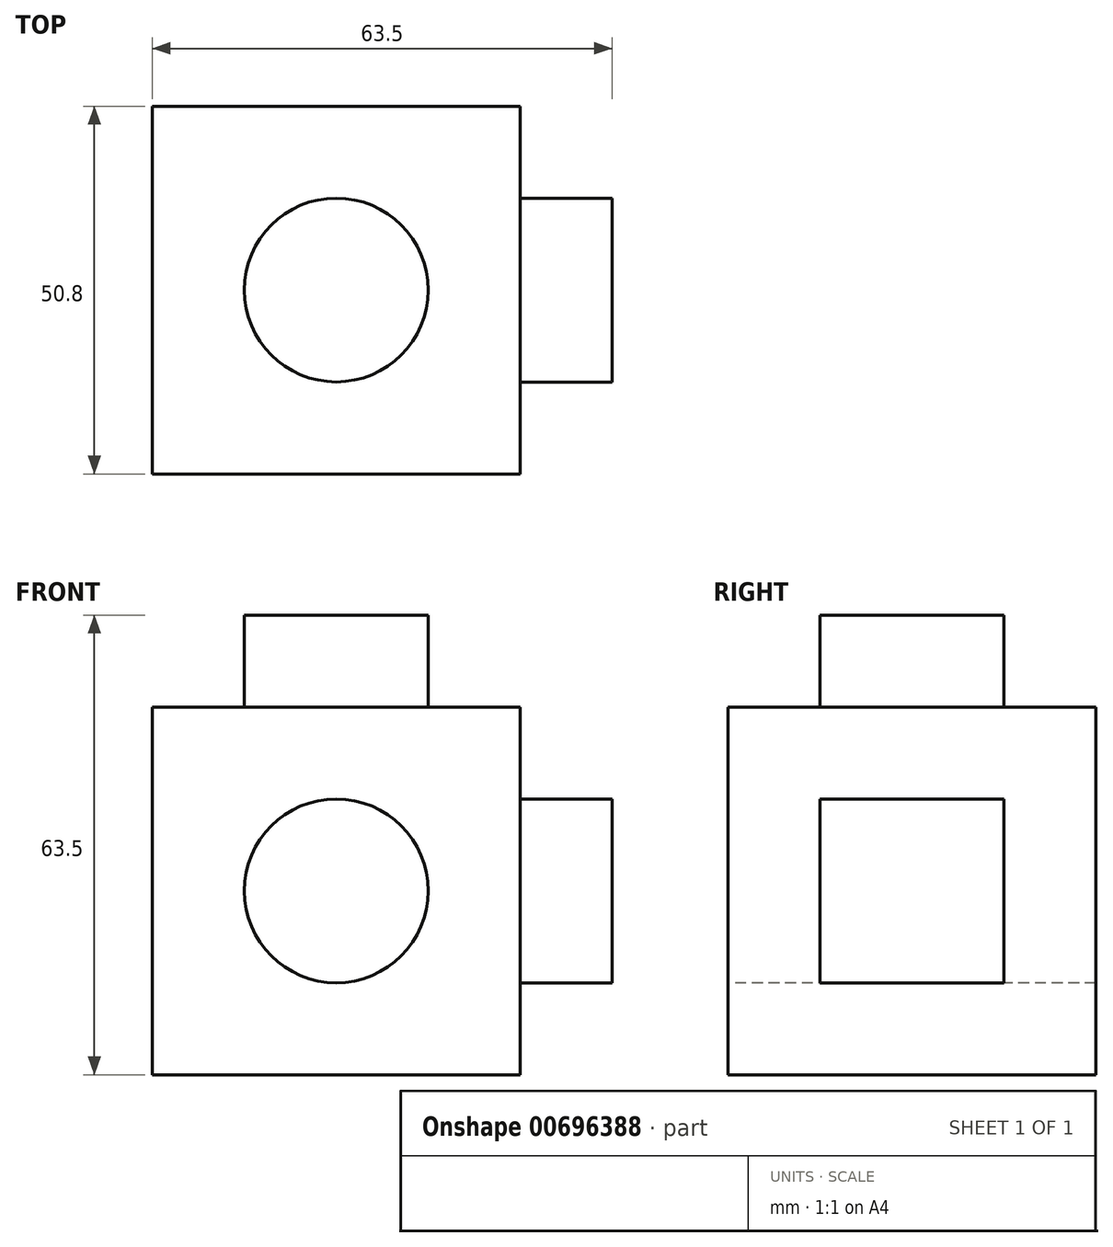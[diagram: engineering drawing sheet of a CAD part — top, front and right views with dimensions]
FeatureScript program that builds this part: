
annotation { "Feature Type Name" : "Feature", "Feature Type Description" : "" }
export const myFeature = defineFeature(function(context is Context, id is Id, definition is map)
    precondition{}
    {
        {
            var Q0;
            Q0=qCreatedBy(makeId("Front.planeOp"),FACE);
            var sketch = newSketch(context, id + "F0", { "sketchPlane" : qUnion([Q0])});
            skLineSegment(sketch, "E0.bottom", {"start": v(0, 0) * mm, "end": v(-50.8, 0) * mm});
            skLineSegment(sketch, "E0.top", {"start": v(0, 50.8) * mm, "end": v(-50.8, 50.8) * mm});
            skLineSegment(sketch, "E0.left", {"start": v(0, 0) * mm, "end": v(0, 50.8) * mm});
            skLineSegment(sketch, "E0.right", {"start": v(-50.8, 0) * mm, "end": v(-50.8, 50.8) * mm});
            skSolve(sketch);
        }
        {
            var Q0;
            Q0=makeQuery(id+"F0.imprint","IMPRINT",FACE,{"disambiguationData":[TD([[makeQuery(id+"F0.imprint","IMPRINT",EDGE,{"derivedFrom":sQuery(id+"F0.wireOp",EDGE,"E0.bottom")}),-1.0]])]});
            extrude(context, id + "F1", {"entities" : qUnion([Q0]), "depth" : 50.8 * mm, "offsetDistance" : 25.4 * mm});
        }
        {
            var Q0;
            Q0=makeQuery(id+"F1.opExtrude","SWEPT_FACE",FACE,{"disambiguationData":[OSD([sQuery(id+"F0.wireOp",EDGE,"E0.top")])]});
            var sketch = newSketch(context, id + "F2", { "sketchPlane" : qUnion([Q0])});
            skCircle(sketch, "E1", {"center": v(-25.4, -25.4) * mm, "radius": 12.7 * mm});
            skSolve(sketch);
        }
        {
            var Q0;
            Q0=makeQuery(id+"F2.imprint","IMPRINT",FACE,{"disambiguationData":[TD([[makeQuery(id+"F2.imprint","IMPRINT",EDGE,{"derivedFrom":sQuery(id+"F2.wireOp",EDGE,"E1")}),1.0]])]});
            extrude(context, id + "F3", {"entities" : qUnion([Q0]), "operationType" : NewBodyOperationType.ADD, "depth" : 12.7 * mm, "offsetDistance" : 25.4 * mm});
        }
        {
            var Q0;
            Q0=makeQuery(id+"F1.opExtrude","SWEPT_FACE",FACE,{"disambiguationData":[OSD([sQuery(id+"F0.wireOp",EDGE,"E0.left")])]});
            var sketch = newSketch(context, id + "F4", { "sketchPlane" : qUnion([Q0])});
            skLineSegment(sketch, "E2.bottom", {"start": v(-12.7, 12.7) * mm, "end": v(-38.1, 12.7) * mm});
            skLineSegment(sketch, "E2.top", {"start": v(-12.7, 38.1) * mm, "end": v(-38.1, 38.1) * mm});
            skLineSegment(sketch, "E2.left", {"start": v(-12.7, 12.7) * mm, "end": v(-12.7, 38.1) * mm});
            skLineSegment(sketch, "E2.right", {"start": v(-38.1, 12.7) * mm, "end": v(-38.1, 38.1) * mm});
            skSolve(sketch);
        }
        {
            var Q0;
            Q0=makeQuery(id+"F4.imprint","IMPRINT",FACE,{"disambiguationData":[TD([[makeQuery(id+"F4.imprint","IMPRINT",EDGE,{"derivedFrom":sQuery(id+"F4.wireOp",EDGE,"E2.bottom")}),-1.0]])]});
            extrude(context, id + "F5", {"entities" : qUnion([Q0]), "operationType" : NewBodyOperationType.ADD, "depth" : 12.7 * mm, "offsetDistance" : 25.4 * mm});
        }
        {
            var Q0;
            Q0=makeQuery(id+"F1.opExtrude","CAP_FACE",FACE,{"disambiguationData":[OSD([sQuery(id+"F0.wireOp",EDGE,"E0.bottom"),sQuery(id+"F0.wireOp",EDGE,"E0.top"),sQuery(id+"F0.wireOp",EDGE,"E0.left"),sQuery(id+"F0.wireOp",EDGE,"E0.right")])],"isStart":false});
            var sketch = newSketch(context, id + "F6", { "sketchPlane" : qUnion([Q0])});
            skCircle(sketch, "E3", {"center": v(-25.4, 25.4) * mm, "radius": 12.7 * mm});
            skSolve(sketch);
        }
        {
            var Q0;
            Q0=makeQuery(id+"F6.imprint","IMPRINT",FACE,{"disambiguationData":[TD([[makeQuery(id+"F6.imprint","IMPRINT",EDGE,{"derivedFrom":sQuery(id+"F6.wireOp",EDGE,"E3")}),1.0]])]});
            extrude(context, id + "F7", {"entities" : qUnion([Q0]), "operationType" : NewBodyOperationType.REMOVE, "oppositeDirection" : true, "depth" : 75.44 * mm, "offsetDistance" : 25.4 * mm});
        }
    });
